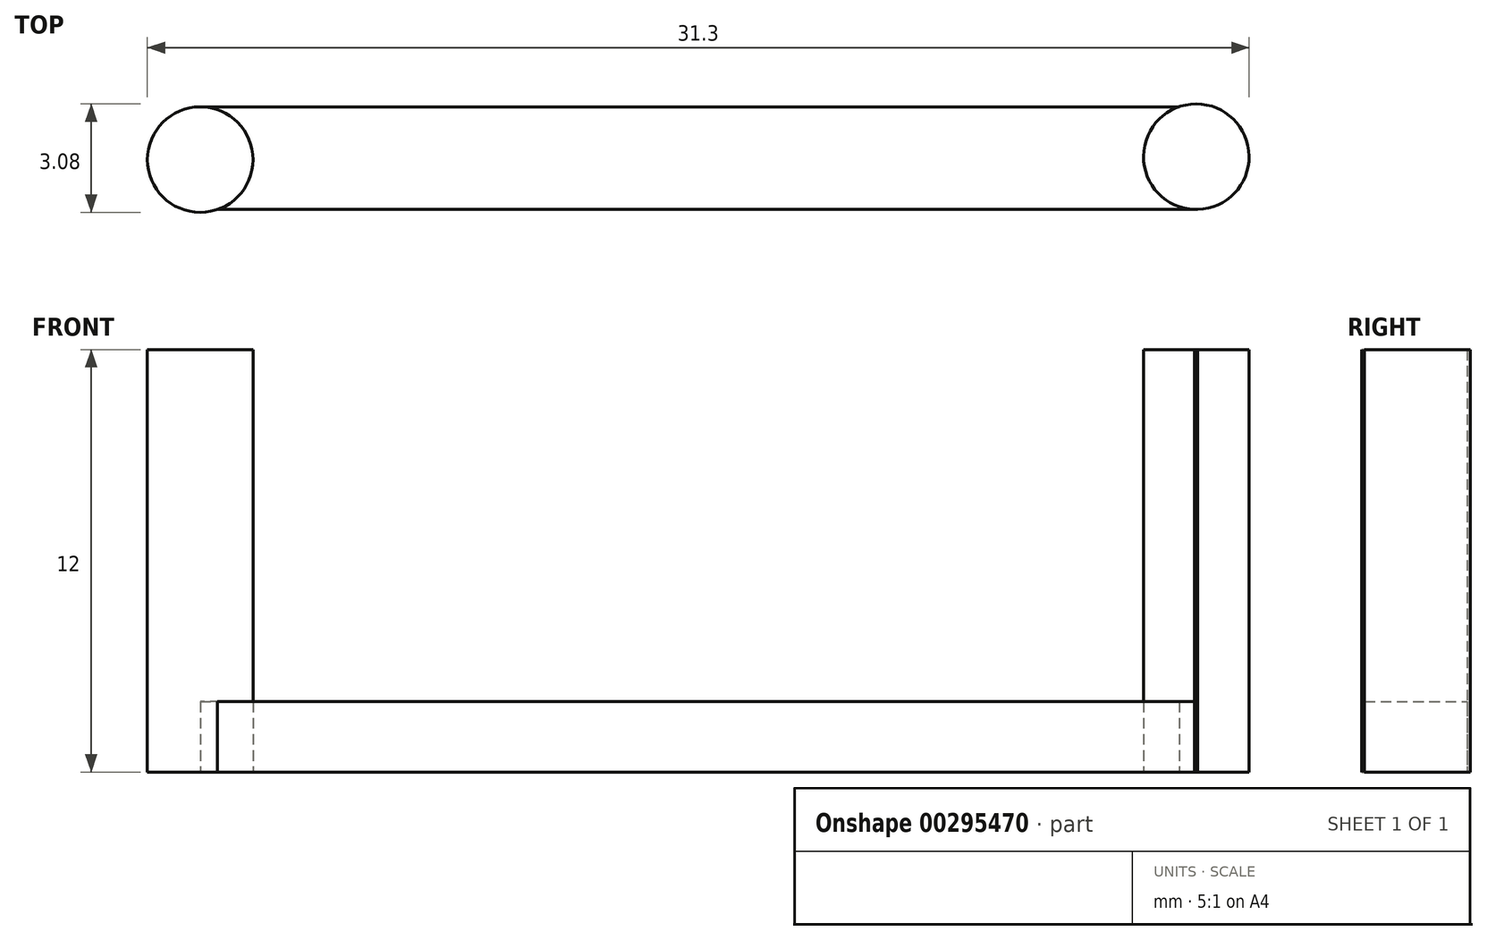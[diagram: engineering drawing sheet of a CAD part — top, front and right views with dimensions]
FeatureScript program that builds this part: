
annotation { "Feature Type Name" : "Feature", "Feature Type Description" : "" }
export const myFeature = defineFeature(function(context is Context, id is Id, definition is map)
    precondition{}
    {
        {
            var Q0;
            Q0=qCreatedBy(makeId("Top.planeOp"),FACE);
            var sketch = newSketch(context, id + "F0", { "sketchPlane" : qUnion([Q0])});
            skCircle(sketch, "E0", {"center": v(0, 0) * mm, "radius": 1.5 * mm});
            skCircle(sketch, "E1", {"center": v(28.3, 0.08) * mm, "radius": 1.5 * mm});
            skLineSegment(sketch, "E2.bottom", {"start": v(0, 1.5) * mm, "end": v(28.34, 1.5) * mm});
            skLineSegment(sketch, "E2.top", {"start": v(0, -1.42) * mm, "end": v(28.34, -1.42) * mm});
            skLineSegment(sketch, "E2.left", {"start": v(0, 1.5) * mm, "end": v(0, -1.42) * mm});
            skLineSegment(sketch, "E2.right", {"start": v(28.34, 1.5) * mm, "end": v(28.34, -1.42) * mm});
            skSolve(sketch);
        }
        {
            var Q0;
            {var subQ0=sQuery(id+"F0.wireOp",EDGE,"E2.left");Q0=makeQuery(id+"F0.imprint","IMPRINT",FACE,{"disambiguationData":[TD([[makeQuery(id+"F0.imprint","IMPRINT",EDGE,{"derivedFrom":subQ0}),1.0]])]});}
            var Q1;
            {var subQ0=sQuery(id+"F0.wireOp",EDGE,"E2.left");Q1=makeQuery(id+"F0.imprint","IMPRINT",FACE,{"disambiguationData":[TD([[makeQuery(id+"F0.imprint","IMPRINT",EDGE,{"derivedFrom":subQ0}),-1.0]])]});}
            var Q2;
            {var subQ0=sQuery(id+"F0.wireOp",EDGE,"E2.right");Q2=makeQuery(id+"F0.imprint","IMPRINT",FACE,{"disambiguationData":[TD([[makeQuery(id+"F0.imprint","IMPRINT",EDGE,{"derivedFrom":subQ0}),1.0]])]});}
            var Q3;
            {var subQ5=sQuery(id+"F0.wireOp",EDGE,"E2.right");Q3=makeQuery(id+"F0.imprint","IMPRINT",FACE,{"disambiguationData":[TD([[makeQuery(id+"F0.imprint","IMPRINT",EDGE,{"derivedFrom":subQ5}),-1.0]])]});}
            extrude(context, id + "F1", {"entities" : qUnion([Q0, Q1, Q2, Q3]), "depth" : 12 * mm});
        }
        {
            var Q0;
            {var subQ3=sQuery(id+"F0.wireOp",EDGE,"E2.top");var subQ5=sQuery(id+"F0.wireOp",EDGE,"E1");var subQ6=makeQuery(id+"F0.imprint","INTERSECT",VERTEX,{"derivedFrom":[subQ5,subQ3]});Q0=makeQuery(id+"F0.imprint","IMPRINT",FACE,{"disambiguationData":[TD([[makeQuery(id+"F0.imprint","IMPRINT",EDGE,{"disambiguationData":[TD([[subQ6,1.0]])],"derivedFrom":subQ5}),-1.0]])]});}
            extrude(context, id + "F2", {"entities" : qUnion([Q0]), "depth" : 2 * mm});
        }
    });
